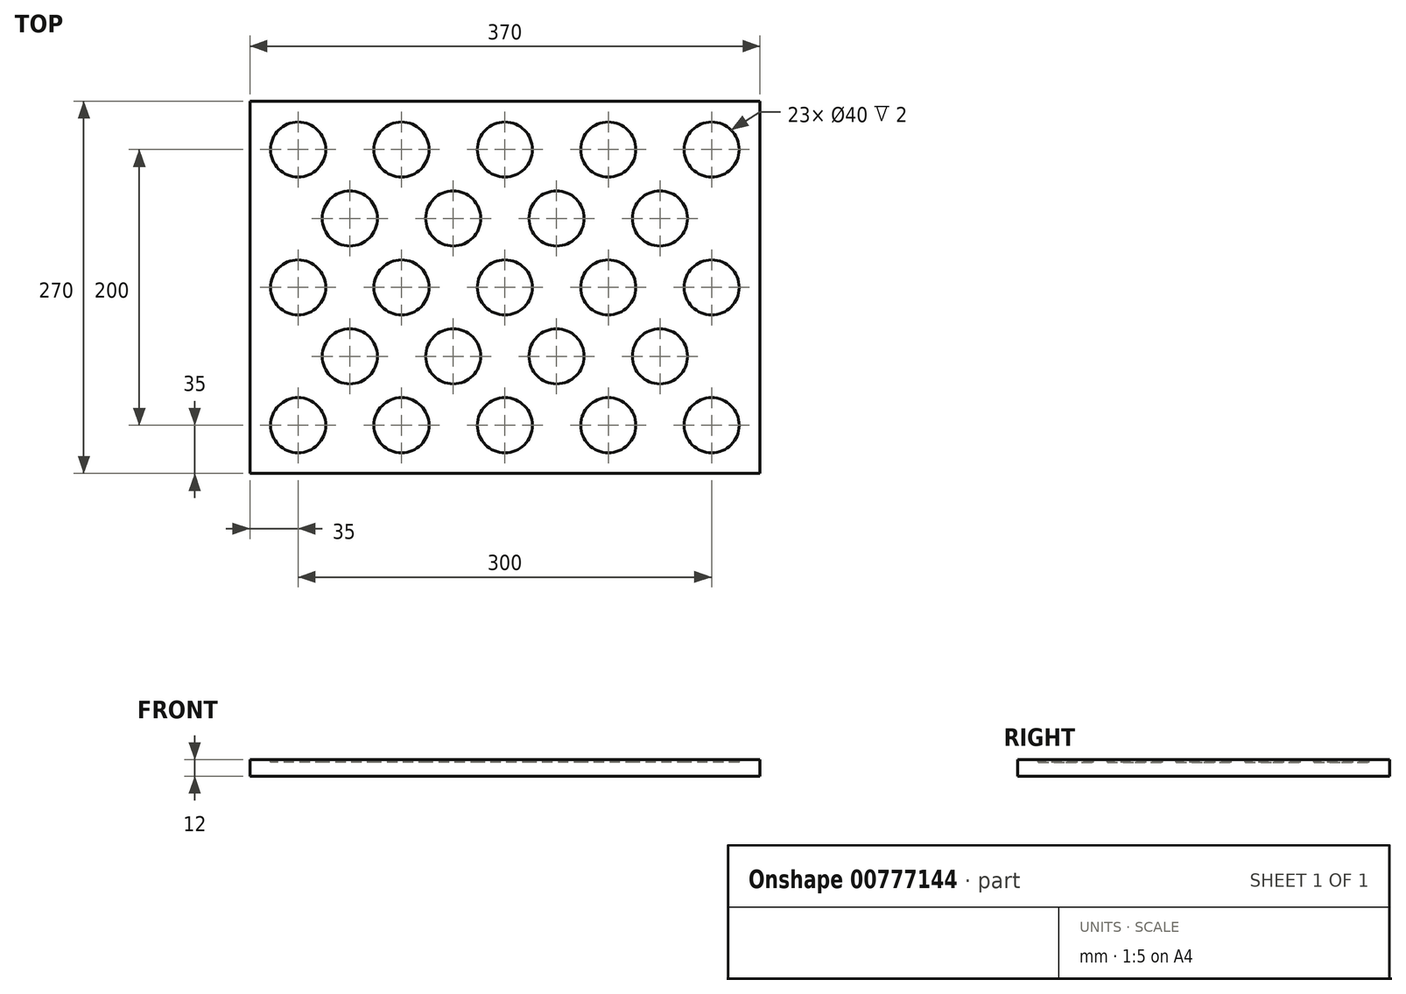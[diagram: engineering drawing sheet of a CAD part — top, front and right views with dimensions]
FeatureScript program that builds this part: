
annotation { "Feature Type Name" : "Feature", "Feature Type Description" : "" }
export const myFeature = defineFeature(function(context is Context, id is Id, definition is map)
    precondition{}
    {
        {
            var Q0;
            Q0=qCreatedBy(makeId("Top.planeOp"),FACE);
            var sketch = newSketch(context, id + "F0", { "sketchPlane" : qUnion([Q0])});
            skCircle(sketch, "E0", {"center": v(0, 0) * mm, "radius": 20 * mm});
            skCircle(sketch, "E1.0.1.0", {"center": v(0, 100) * mm, "radius": 20 * mm});
            skCircle(sketch, "E1.0.2.0", {"center": v(0, 200) * mm, "radius": 20 * mm});
            skCircle(sketch, "E1.1.0.0", {"center": v(75, 0) * mm, "radius": 20 * mm});
            skCircle(sketch, "E1.1.1.0", {"center": v(75, 100) * mm, "radius": 20 * mm});
            skCircle(sketch, "E1.1.2.0", {"center": v(75, 200) * mm, "radius": 20 * mm});
            skCircle(sketch, "E1.2.0.0", {"center": v(150, 0) * mm, "radius": 20 * mm});
            skCircle(sketch, "E1.2.1.0", {"center": v(150, 100) * mm, "radius": 20 * mm});
            skCircle(sketch, "E1.2.2.0", {"center": v(150, 200) * mm, "radius": 20 * mm});
            skCircle(sketch, "E1.3.0.0", {"center": v(225, 0) * mm, "radius": 20 * mm});
            skCircle(sketch, "E1.3.1.0", {"center": v(225, 100) * mm, "radius": 20 * mm});
            skCircle(sketch, "E1.3.2.0", {"center": v(225, 200) * mm, "radius": 20 * mm});
            skCircle(sketch, "E1.4.0.0", {"center": v(300, 0) * mm, "radius": 20 * mm});
            skCircle(sketch, "E1.4.1.0", {"center": v(300, 100) * mm, "radius": 20 * mm});
            skCircle(sketch, "E1.4.2.0", {"center": v(300, 200) * mm, "radius": 20 * mm});
            skLineSegment(sketch, "E1.direction1", {"start": v(0, 0) * mm, "end": v(75, 0) * mm, "construction": true});
            skLineSegment(sketch, "E1.direction2", {"start": v(0, 0) * mm, "end": v(0, 100) * mm, "construction": true});
            skLineSegment(sketch, "E2", {"start": v(75, 0) * mm, "end": v(0, 100) * mm});
            skCircle(sketch, "E3", {"center": v(37.5, 50) * mm, "radius": 20 * mm});
            skCircle(sketch, "E4.0.1.0", {"center": v(37.5, 150) * mm, "radius": 20 * mm});
            skCircle(sketch, "E4.1.0.0", {"center": v(112.5, 50) * mm, "radius": 20 * mm});
            skCircle(sketch, "E4.1.1.0", {"center": v(112.5, 150) * mm, "radius": 20 * mm});
            skCircle(sketch, "E4.2.0.0", {"center": v(187.5, 50) * mm, "radius": 20 * mm});
            skCircle(sketch, "E4.2.1.0", {"center": v(187.5, 150) * mm, "radius": 20 * mm});
            skCircle(sketch, "E4.3.0.0", {"center": v(262.5, 50) * mm, "radius": 20 * mm});
            skCircle(sketch, "E4.3.1.0", {"center": v(262.5, 150) * mm, "radius": 20 * mm});
            skLineSegment(sketch, "E4.direction1", {"start": v(37.5, 50) * mm, "end": v(112.5, 50) * mm, "construction": true});
            skLineSegment(sketch, "E4.direction2", {"start": v(37.5, 50) * mm, "end": v(37.5, 150) * mm, "construction": true});
            skSolve(sketch);
        }
        {
            var Q0;
            Q0=makeQuery(id+"F0.imprint","IMPRINT",FACE,{"disambiguationData":[TD([[makeQuery(id+"F0.imprint","IMPRINT",EDGE,{"derivedFrom":sQuery(id+"F0.wireOp",EDGE,"E1.0.2.0")}),1.0]])]});
            var Q1;
            Q1=makeQuery(id+"F0.imprint","IMPRINT",FACE,{"disambiguationData":[TD([[makeQuery(id+"F0.imprint","IMPRINT",EDGE,{"derivedFrom":sQuery(id+"F0.wireOp",EDGE,"E1.1.2.0")}),1.0]])]});
            var Q2;
            Q2=makeQuery(id+"F0.imprint","IMPRINT",FACE,{"disambiguationData":[TD([[makeQuery(id+"F0.imprint","IMPRINT",EDGE,{"derivedFrom":sQuery(id+"F0.wireOp",EDGE,"E1.2.2.0")}),1.0]])]});
            var Q3;
            Q3=makeQuery(id+"F0.imprint","IMPRINT",FACE,{"disambiguationData":[TD([[makeQuery(id+"F0.imprint","IMPRINT",EDGE,{"derivedFrom":sQuery(id+"F0.wireOp",EDGE,"E1.3.2.0")}),1.0]])]});
            var Q4;
            Q4=makeQuery(id+"F0.imprint","IMPRINT",FACE,{"disambiguationData":[TD([[makeQuery(id+"F0.imprint","IMPRINT",EDGE,{"derivedFrom":sQuery(id+"F0.wireOp",EDGE,"E1.4.2.0")}),1.0]])]});
            var Q5;
            Q5=makeQuery(id+"F0.imprint","IMPRINT",FACE,{"disambiguationData":[TD([[makeQuery(id+"F0.imprint","IMPRINT",EDGE,{"derivedFrom":sQuery(id+"F0.wireOp",EDGE,"E4.3.1.0")}),1.0]])]});
            var Q6;
            Q6=makeQuery(id+"F0.imprint","IMPRINT",FACE,{"disambiguationData":[TD([[makeQuery(id+"F0.imprint","IMPRINT",EDGE,{"derivedFrom":sQuery(id+"F0.wireOp",EDGE,"E1.4.1.0")}),1.0]])]});
            var Q7;
            Q7=makeQuery(id+"F0.imprint","IMPRINT",FACE,{"disambiguationData":[TD([[makeQuery(id+"F0.imprint","IMPRINT",EDGE,{"derivedFrom":sQuery(id+"F0.wireOp",EDGE,"E1.4.0.0")}),1.0]])]});
            var Q8;
            Q8=makeQuery(id+"F0.imprint","IMPRINT",FACE,{"disambiguationData":[TD([[makeQuery(id+"F0.imprint","IMPRINT",EDGE,{"derivedFrom":sQuery(id+"F0.wireOp",EDGE,"E4.2.1.0")}),1.0]])]});
            var Q9;
            Q9=makeQuery(id+"F0.imprint","IMPRINT",FACE,{"disambiguationData":[TD([[makeQuery(id+"F0.imprint","IMPRINT",EDGE,{"derivedFrom":sQuery(id+"F0.wireOp",EDGE,"E4.1.1.0")}),1.0]])]});
            var Q10;
            Q10=makeQuery(id+"F0.imprint","IMPRINT",FACE,{"disambiguationData":[TD([[makeQuery(id+"F0.imprint","IMPRINT",EDGE,{"derivedFrom":sQuery(id+"F0.wireOp",EDGE,"E4.0.1.0")}),1.0]])]});
            var Q11;
            Q11=makeQuery(id+"F0.imprint","IMPRINT",FACE,{"disambiguationData":[TD([[makeQuery(id+"F0.imprint","IMPRINT",EDGE,{"derivedFrom":sQuery(id+"F0.wireOp",EDGE,"E1.0.1.0")}),1.0]])]});
            var Q12;
            Q12=makeQuery(id+"F0.imprint","IMPRINT",FACE,{"disambiguationData":[TD([[makeQuery(id+"F0.imprint","IMPRINT",EDGE,{"derivedFrom":sQuery(id+"F0.wireOp",EDGE,"E1.1.1.0")}),1.0]])]});
            var Q13;
            Q13=makeQuery(id+"F0.imprint","IMPRINT",FACE,{"disambiguationData":[TD([[makeQuery(id+"F0.imprint","IMPRINT",EDGE,{"derivedFrom":sQuery(id+"F0.wireOp",EDGE,"E1.2.1.0")}),1.0]])]});
            var Q14;
            Q14=makeQuery(id+"F0.imprint","IMPRINT",FACE,{"disambiguationData":[TD([[makeQuery(id+"F0.imprint","IMPRINT",EDGE,{"derivedFrom":sQuery(id+"F0.wireOp",EDGE,"E1.3.1.0")}),1.0]])]});
            var Q15;
            Q15=makeQuery(id+"F0.imprint","IMPRINT",FACE,{"disambiguationData":[TD([[makeQuery(id+"F0.imprint","IMPRINT",EDGE,{"derivedFrom":sQuery(id+"F0.wireOp",EDGE,"E4.3.0.0")}),1.0]])]});
            var Q16;
            Q16=makeQuery(id+"F0.imprint","IMPRINT",FACE,{"disambiguationData":[TD([[makeQuery(id+"F0.imprint","IMPRINT",EDGE,{"derivedFrom":sQuery(id+"F0.wireOp",EDGE,"E4.2.0.0")}),1.0]])]});
            var Q17;
            Q17=makeQuery(id+"F0.imprint","IMPRINT",FACE,{"disambiguationData":[TD([[makeQuery(id+"F0.imprint","IMPRINT",EDGE,{"derivedFrom":sQuery(id+"F0.wireOp",EDGE,"E1.3.0.0")}),1.0]])]});
            var Q18;
            Q18=makeQuery(id+"F0.imprint","IMPRINT",FACE,{"disambiguationData":[TD([[makeQuery(id+"F0.imprint","IMPRINT",EDGE,{"derivedFrom":sQuery(id+"F0.wireOp",EDGE,"E1.2.0.0")}),1.0]])]});
            var Q19;
            Q19=makeQuery(id+"F0.imprint","IMPRINT",FACE,{"disambiguationData":[TD([[makeQuery(id+"F0.imprint","IMPRINT",EDGE,{"derivedFrom":sQuery(id+"F0.wireOp",EDGE,"E4.1.0.0")}),1.0]])]});
            var Q20;
            {var subQ0=sQuery(id+"F0.wireOp",EDGE,"E3");var subQ1=sQuery(id+"F0.wireOp",EDGE,"E2");var subQ2=makeQuery(id+"F0.imprint","INTERSECT",VERTEX,{"disambiguationData":[OD(0.0)],"derivedFrom":[subQ1,subQ0]});Q20=makeQuery(id+"F0.imprint","IMPRINT",FACE,{"disambiguationData":[TD([[makeQuery(id+"F0.imprint","IMPRINT",EDGE,{"disambiguationData":[TD([[subQ2,1.0]])],"derivedFrom":subQ1}),-1.0]])]});}
            var Q21;
            Q21=makeQuery(id+"F0.imprint","IMPRINT",FACE,{"disambiguationData":[TD([[makeQuery(id+"F0.imprint","IMPRINT",EDGE,{"derivedFrom":sQuery(id+"F0.wireOp",EDGE,"E0")}),1.0]])]});
            var Q22;
            Q22=makeQuery(id+"F0.imprint","IMPRINT",FACE,{"disambiguationData":[TD([[makeQuery(id+"F0.imprint","IMPRINT",EDGE,{"derivedFrom":sQuery(id+"F0.wireOp",EDGE,"E1.1.0.0")}),1.0]])]});
            var Q23;
            {var subQ0=sQuery(id+"F0.wireOp",EDGE,"E3");var subQ1=sQuery(id+"F0.wireOp",EDGE,"E2");var subQ2=makeQuery(id+"F0.imprint","INTERSECT",VERTEX,{"disambiguationData":[OD(0.0)],"derivedFrom":[subQ1,subQ0]});Q23=makeQuery(id+"F0.imprint","IMPRINT",FACE,{"disambiguationData":[TD([[makeQuery(id+"F0.imprint","IMPRINT",EDGE,{"disambiguationData":[TD([[subQ2,1.0]])],"derivedFrom":subQ1}),1.0]])]});}
            extrude(context, id + "F1", {"entities" : qUnion([Q0, Q1, Q2, Q3, Q4, Q5, Q6, Q7, Q8, Q9, Q10, Q11, Q12, Q13, Q14, Q15, Q16, Q17, Q18, Q19, Q20, Q21, Q22, Q23]), "oppositeDirection" : true, "depth" : 2 * mm, "offsetDistance" : 25 * mm});
        }
        {
            var Q0;
            Q0=qCreatedBy(makeId("Top.planeOp"),FACE);
            var sketch = newSketch(context, id + "F2", { "sketchPlane" : qUnion([Q0])});
            skLineSegment(sketch, "E5.bottom", {"start": v(-35, 235) * mm, "end": v(335, 235) * mm});
            skLineSegment(sketch, "E5.top", {"start": v(-35, -35) * mm, "end": v(335, -35) * mm});
            skLineSegment(sketch, "E5.left", {"start": v(-35, 235) * mm, "end": v(-35, -35) * mm});
            skLineSegment(sketch, "E5.right", {"start": v(335, 235) * mm, "end": v(335, -35) * mm});
            skSolve(sketch);
        }
        {
            var Q0;
            Q0=makeQuery(id+"F2.imprint","IMPRINT",FACE,{"disambiguationData":[TD([[makeQuery(id+"F2.imprint","IMPRINT",EDGE,{"derivedFrom":sQuery(id+"F2.wireOp",EDGE,"E5.bottom")}),-1.0]])]});
            extrude(context, id + "F3", {"entities" : qUnion([Q0]), "oppositeDirection" : true, "depth" : 12 * mm, "offsetDistance" : 25 * mm});
        }
        {
            var Q0;
            Q0=makeQuery(id+"F1.opExtrude","SWEPT_BODY",BODY,{"disambiguationData":[OSD([sQuery(id+"F0.wireOp",EDGE,"E1.0.2.0")])]});
            var Q1;
            Q1=makeQuery(id+"F1.opExtrude","SWEPT_BODY",BODY,{"disambiguationData":[OSD([sQuery(id+"F0.wireOp",EDGE,"E1.1.2.0")])]});
            var Q2;
            Q2=makeQuery(id+"F1.opExtrude","SWEPT_BODY",BODY,{"disambiguationData":[OSD([sQuery(id+"F0.wireOp",EDGE,"E1.2.2.0")])]});
            var Q3;
            Q3=makeQuery(id+"F1.opExtrude","SWEPT_BODY",BODY,{"disambiguationData":[OSD([sQuery(id+"F0.wireOp",EDGE,"E1.4.2.0")])]});
            var Q4;
            Q4=makeQuery(id+"F1.opExtrude","SWEPT_BODY",BODY,{"disambiguationData":[OSD([sQuery(id+"F0.wireOp",EDGE,"E1.3.2.0")])]});
            var Q5;
            Q5=makeQuery(id+"F1.opExtrude","SWEPT_BODY",BODY,{"disambiguationData":[OSD([sQuery(id+"F0.wireOp",EDGE,"E4.0.1.0")])]});
            var Q6;
            Q6=makeQuery(id+"F1.opExtrude","SWEPT_BODY",BODY,{"disambiguationData":[OSD([sQuery(id+"F0.wireOp",EDGE,"E4.1.1.0")])]});
            var Q7;
            Q7=makeQuery(id+"F1.opExtrude","SWEPT_BODY",BODY,{"disambiguationData":[OSD([sQuery(id+"F0.wireOp",EDGE,"E4.2.1.0")])]});
            var Q8;
            Q8=makeQuery(id+"F1.opExtrude","SWEPT_BODY",BODY,{"disambiguationData":[OSD([sQuery(id+"F0.wireOp",EDGE,"E4.3.1.0")])]});
            var Q9;
            Q9=makeQuery(id+"F1.opExtrude","SWEPT_BODY",BODY,{"disambiguationData":[OSD([sQuery(id+"F0.wireOp",EDGE,"E1.4.1.0")])]});
            var Q10;
            Q10=makeQuery(id+"F1.opExtrude","SWEPT_BODY",BODY,{"disambiguationData":[OSD([sQuery(id+"F0.wireOp",EDGE,"E1.0.1.0")])]});
            var Q11;
            Q11=makeQuery(id+"F1.opExtrude","SWEPT_BODY",BODY,{"disambiguationData":[OSD([sQuery(id+"F0.wireOp",EDGE,"E1.1.1.0")])]});
            var Q12;
            Q12=makeQuery(id+"F1.opExtrude","SWEPT_BODY",BODY,{"disambiguationData":[OSD([sQuery(id+"F0.wireOp",EDGE,"E1.3.1.0")])]});
            var Q13;
            Q13=makeQuery(id+"F1.opExtrude","SWEPT_BODY",BODY,{"disambiguationData":[OSD([sQuery(id+"F0.wireOp",EDGE,"E4.3.0.0")])]});
            var Q14;
            Q14=makeQuery(id+"F1.opExtrude","SWEPT_BODY",BODY,{"disambiguationData":[OSD([sQuery(id+"F0.wireOp",EDGE,"E1.4.0.0")])]});
            var Q15;
            Q15=makeQuery(id+"F1.opExtrude","SWEPT_BODY",BODY,{"disambiguationData":[OSD([sQuery(id+"F0.wireOp",EDGE,"E1.3.0.0")])]});
            var Q16;
            Q16=makeQuery(id+"F1.opExtrude","SWEPT_BODY",BODY,{"disambiguationData":[OSD([sQuery(id+"F0.wireOp",EDGE,"E4.2.0.0")])]});
            var Q17;
            Q17=makeQuery(id+"F1.opExtrude","SWEPT_BODY",BODY,{"disambiguationData":[OSD([sQuery(id+"F0.wireOp",EDGE,"E1.2.0.0")])]});
            var Q18;
            Q18=makeQuery(id+"F1.opExtrude","SWEPT_BODY",BODY,{"disambiguationData":[OSD([sQuery(id+"F0.wireOp",EDGE,"E4.1.0.0")])]});
            var Q19;
            Q19=makeQuery(id+"F1.opExtrude","SWEPT_BODY",BODY,{"disambiguationData":[OSD([sQuery(id+"F0.wireOp",EDGE,"E1.1.0.0")])]});
            var Q20;
            Q20=makeQuery(id+"F1.opExtrude","SWEPT_BODY",BODY,{"disambiguationData":[OSD([sQuery(id+"F0.wireOp",EDGE,"E0")])]});
            var Q21;
            Q21=makeQuery(id+"F1.opExtrude","SWEPT_BODY",BODY,{"disambiguationData":[OSD([sQuery(id+"F0.wireOp",EDGE,"E1.2.1.0")])]});
            var Q22;
            Q22=makeQuery(id+"F1.opExtrude","SWEPT_BODY",BODY,{"disambiguationData":[OSD([sQuery(id+"F0.wireOp",EDGE,"E3")])]});
            var Q23;
            Q23=makeQuery(id+"F3.opExtrude","SWEPT_BODY",BODY,{"disambiguationData":[OSD([sQuery(id+"F2.wireOp",EDGE,"E5.bottom"),sQuery(id+"F2.wireOp",EDGE,"E5.top"),sQuery(id+"F2.wireOp",EDGE,"E5.left"),sQuery(id+"F2.wireOp",EDGE,"E5.right")])]});
            booleanBodies(context, id + "F4", {"operationType" : BooleanOperationType.SUBTRACTION, "tools" : qUnion([Q0, Q1, Q2, Q3, Q4, Q5, Q6, Q7, Q8, Q9, Q10, Q11, Q12, Q13, Q14, Q15, Q16, Q17, Q18, Q19, Q20, Q21, Q22]), "targets" : qUnion([Q23])});
        }
    });
